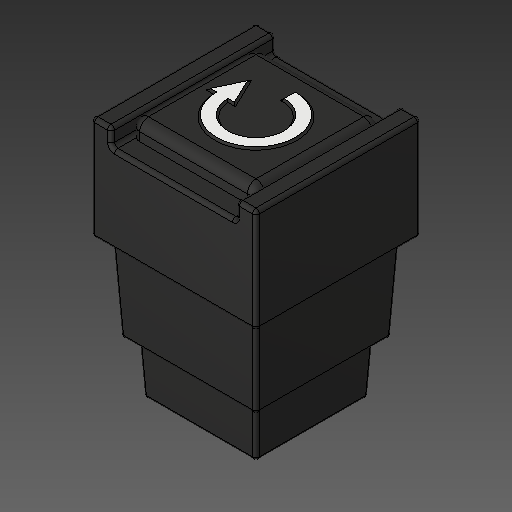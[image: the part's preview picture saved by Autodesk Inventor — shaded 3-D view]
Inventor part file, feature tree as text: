
AUTODESK INVENTOR PART (.ipt)
format: ipt  version: 2018.2 (Build 222227000, 227)  size: 227,840 bytes
history: native  units: mm
features: other x2, fillet x2
ambient origin geometry x8: Origin, YZ Plane, XZ Plane, XY Plane, X Axis, Y Axis, Z Axis, Center Point
bodies: Body1 (feature_tree), Body2 (feature_tree)
feature tree (4):
  other  "ソリッド1"
  other  "ソリッド2"
  fillet  "Fillet1"  [1 undecoded]
  fillet  "Fillet3"  [1 undecoded]
note: 2 required parameter values undecoded (feature->parameter linkage not recoverable at this tier; creation-order binding heuristic only, values carry confidence <= 0.55)
